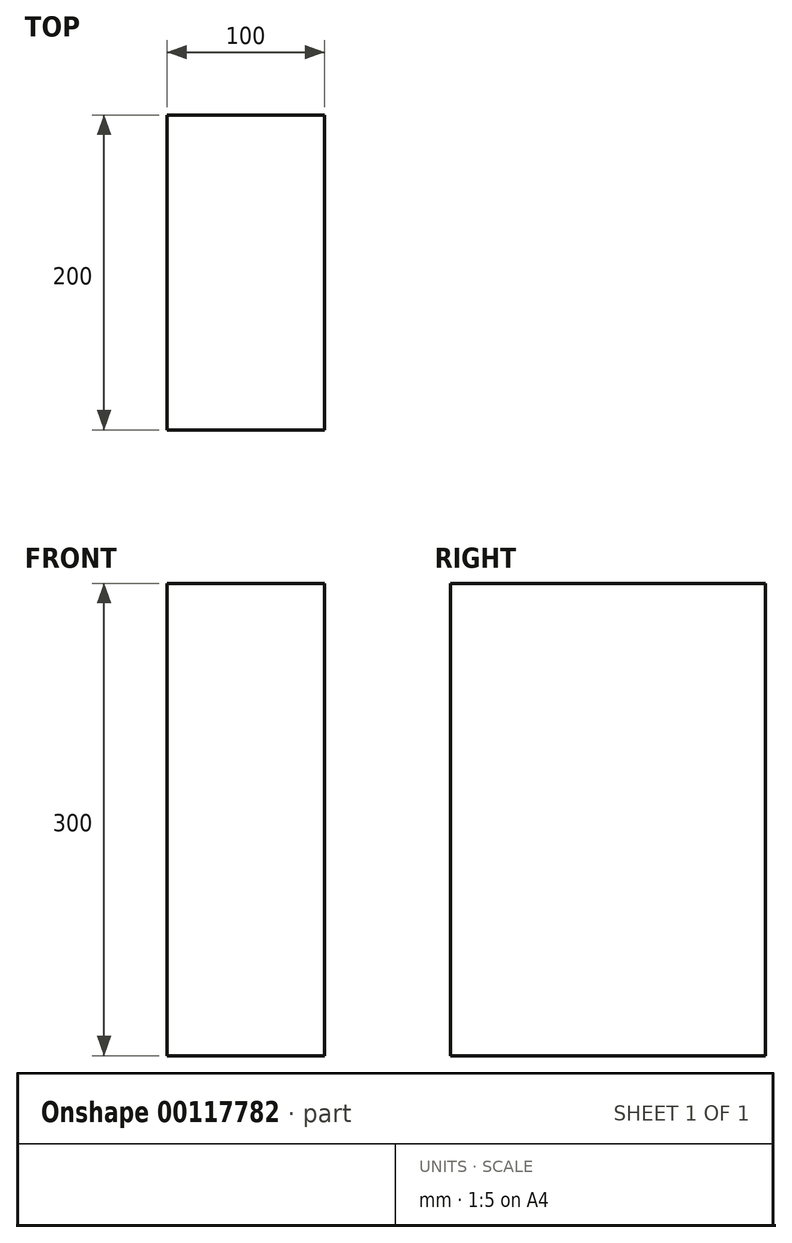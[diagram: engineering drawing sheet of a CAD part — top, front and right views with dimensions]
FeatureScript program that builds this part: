
annotation { "Feature Type Name" : "Feature", "Feature Type Description" : "" }
export const myFeature = defineFeature(function(context is Context, id is Id, definition is map)
    precondition{}
    {
        {
            var Q0;
            Q0=qCreatedBy(makeId("Top.planeOp"),FACE);
            var sketch = newSketch(context, id + "F0", { "sketchPlane" : qUnion([Q0])});
            skLineSegment(sketch, "E0.bottom", {"start": v(0, 0) * mm, "end": v(100, 0) * mm});
            skLineSegment(sketch, "E0.top", {"start": v(0, -200) * mm, "end": v(100, -200) * mm});
            skLineSegment(sketch, "E0.left", {"start": v(0, 0) * mm, "end": v(0, -200) * mm});
            skLineSegment(sketch, "E0.right", {"start": v(100, 0) * mm, "end": v(100, -200) * mm});
            skSolve(sketch);
        }
        {
            var Q0;
            Q0=makeQuery(id+"F0.imprint","IMPRINT",FACE,{"disambiguationData":[TD([[makeQuery(id+"F0.imprint","IMPRINT",EDGE,{"derivedFrom":sQuery(id+"F0.wireOp",EDGE,"E0.bottom")}),-1.0]])]});
            extrude(context, id + "F1", {"entities" : qUnion([Q0]), "oppositeDirection" : true, "depth" : 300 * mm});
        }
    });
